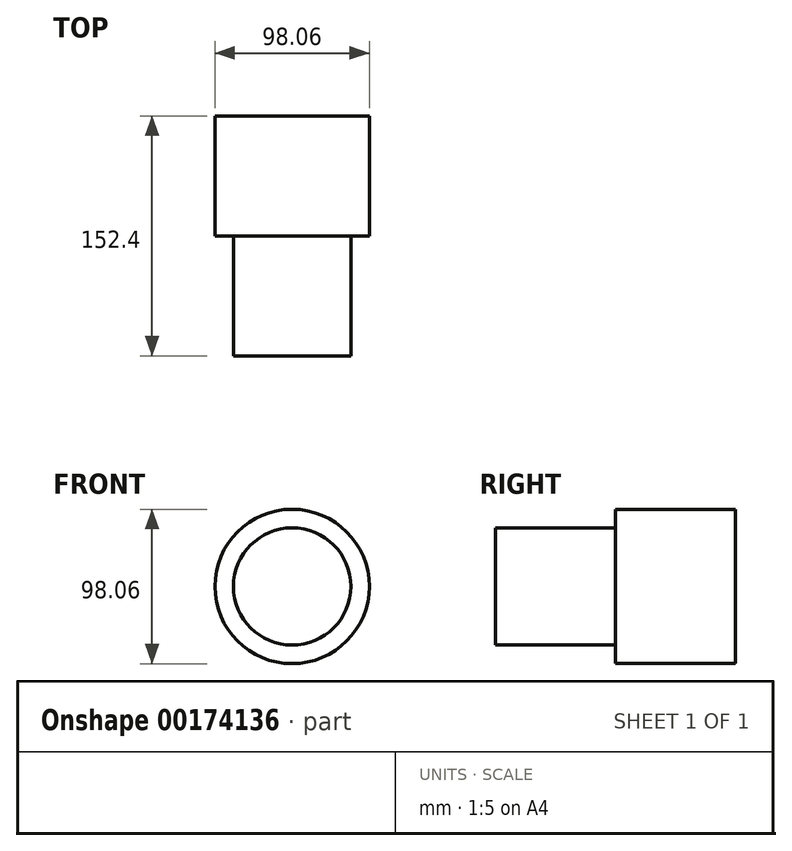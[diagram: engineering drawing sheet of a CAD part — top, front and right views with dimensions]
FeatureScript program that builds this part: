
annotation { "Feature Type Name" : "Feature", "Feature Type Description" : "" }
export const myFeature = defineFeature(function(context is Context, id is Id, definition is map)
    precondition{}
    {
        {
            var Q0;
            Q0=qCreatedBy(makeId("Front.planeOp"),FACE);
            var sketch = newSketch(context, id + "F0", { "sketchPlane" : qUnion([Q0])});
            skCircle(sketch, "E0", {"center": v(0, 0) * mm, "radius": 49.03 * mm});
            skSolve(sketch);
        }
        {
            var Q0;
            Q0 = qSketchRegion(id + "F0", true);
            extrude(context, id + "F1", {"entities" : qUnion([Q0]), "depth" : 76.2 * mm});
        }
        {
            var Q0;
            Q0=qCreatedBy(makeId("Front.planeOp"),FACE);
            var sketch = newSketch(context, id + "F2", { "sketchPlane" : qUnion([Q0])});
            skCircle(sketch, "E1", {"center": v(0, 0) * mm, "radius": 37.26 * mm});
            skSolve(sketch);
        }
        {
            var Q0;
            Q0 = qSketchRegion(id + "F2", true);
            extrude(context, id + "F3", {"entities" : qUnion([Q0]), "operationType" : NewBodyOperationType.ADD, "depth" : 152.4 * mm});
        }
        {
            var Q0;
            Q0=qCreatedBy(makeId("Front.planeOp"),FACE);
            var sketch = newSketch(context, id + "F4", { "sketchPlane" : qUnion([Q0])});
            skCircle(sketch, "E2", {"center": v(0, 0) * mm, "radius": 23.61 * mm});
            skSolve(sketch);
        }
        {
            var Q0;
            Q0 = qSketchRegion(id + "F4", true);
            extrude(context, id + "F5", {"entities" : qUnion([Q0]), "operationType" : NewBodyOperationType.REMOVE, "endBound" : BoundingType.THROUGH_ALL, "oppositeDirection" : true, "depth" : 25.4 * mm});
        }
    });
